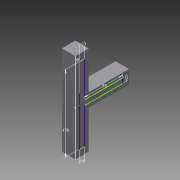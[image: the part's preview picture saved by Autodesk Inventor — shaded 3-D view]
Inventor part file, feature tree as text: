
AUTODESK INVENTOR PART (.ipt)
format: ipt  version: 2015 (Build 190159000, 159)  size: 88,064 bytes
history: native  units: mm
features: sketch x3, other x1, extrude x1
ambient origin geometry x8: Origin, YZ Plane, XZ Plane, XY Plane, X Axis, Y Axis, Z Axis, Center Point
bodies: Body1 (feature_tree)
feature tree (5):
  other  "ソリッド1"
  extrude  "押し出し1"  Depth=30.0mm
  sketch  "スケッチ2"
  sketch  "スケッチ3"
  sketch  "スケッチ1"
